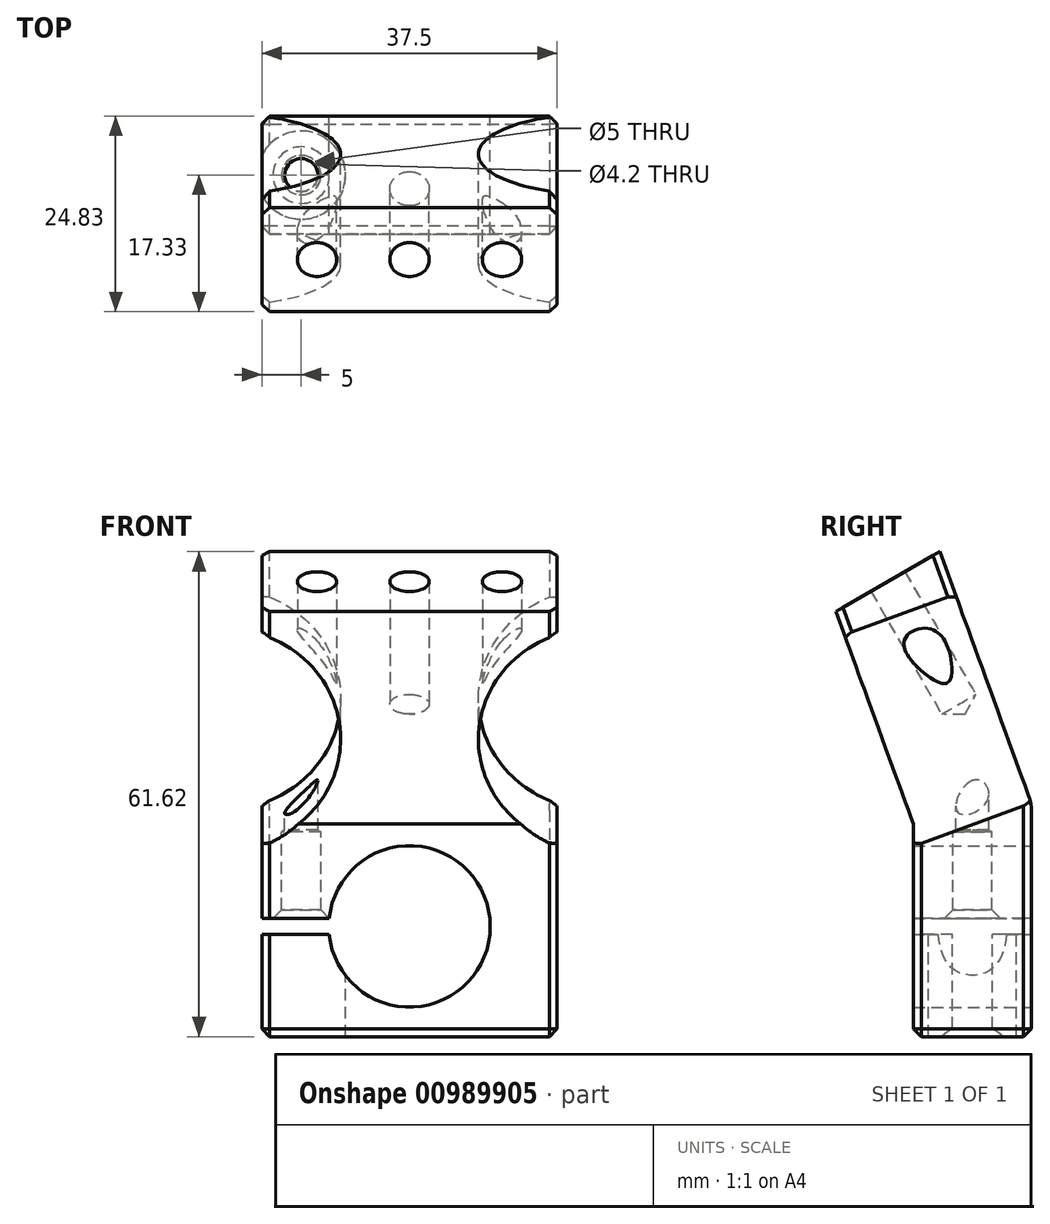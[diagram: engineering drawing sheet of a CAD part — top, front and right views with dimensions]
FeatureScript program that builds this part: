
annotation { "Feature Type Name" : "Feature", "Feature Type Description" : "" }
export const myFeature = defineFeature(function(context is Context, id is Id, definition is map)
    precondition{}
    {
        {
            var Q0;
            Q0=qCreatedBy(makeId("Right.planeOp"),FACE);
            var sketch = newSketch(context, id + "F0", { "sketchPlane" : qUnion([Q0])});
            skLineSegment(sketch, "E0", {"start": v(-9.83, 40) * mm, "end": v(0, 13) * mm});
            skLineSegment(sketch, "E1", {"start": v(0, 13) * mm, "end": v(0, -14) * mm});
            skLineSegment(sketch, "E2", {"start": v(0, -14) * mm, "end": v(15, -14) * mm});
            skLineSegment(sketch, "E3", {"start": v(15, -14) * mm, "end": v(15, 15.64) * mm});
            skLineSegment(sketch, "E4", {"start": v(15, 15.64) * mm, "end": v(3.36, 47.62) * mm});
            skLineSegment(sketch, "E5", {"start": v(-9.83, 40) * mm, "end": v(3.36, 47.62) * mm});
            skSolve(sketch);
        }
        {
            var Q0;
            Q0=makeQuery(id+"F0.imprint","IMPRINT",FACE,{"disambiguationData":[TD([[makeQuery(id+"F0.imprint","IMPRINT",EDGE,{"derivedFrom":sQuery(id+"F0.wireOp",EDGE,"E0")}),1.0]])]});
            extrude(context, id + "F1", {"entities" : qUnion([Q0]), "depth" : 37.5 * mm, "offsetDistance" : 25 * mm, "symmetric" : true});
        }
        {
            var Q0;
            Q0=makeQuery(id+"F1.opExtrude","SWEPT_FACE",FACE,{"disambiguationData":[OSD([sQuery(id+"F0.wireOp",EDGE,"E1")])]});
            var sketch = newSketch(context, id + "F2", { "sketchPlane" : qUnion([Q0])});
            skPoint(sketch, "E6", {"position": v(0, 0) * mm});
            skLineSegment(sketch, "E7.bottom", {"start": v(-18.75, 1) * mm, "end": v(-8.7, 1) * mm});
            skLineSegment(sketch, "E7.top", {"start": v(-18.75, -1) * mm, "end": v(-8.7, -1) * mm});
            skLineSegment(sketch, "E7.left", {"start": v(-18.75, 1) * mm, "end": v(-18.75, -1) * mm});
            skLineSegment(sketch, "E7.right", {"start": v(-8.7, 1) * mm, "end": v(-8.7, -1) * mm});
            skSolve(sketch);
        }
        {
            var Q0;
            Q0=sQuery(id+"F2.wireOp",VERTEX,"E6");
            var Q1;
            Q1=makeQuery(id+"F1.opExtrude","SWEPT_BODY",BODY,{"disambiguationData":[OSD([sQuery(id+"F0.wireOp",EDGE,"E0"),sQuery(id+"F0.wireOp",EDGE,"E1"),sQuery(id+"F0.wireOp",EDGE,"E2"),sQuery(id+"F0.wireOp",EDGE,"E3"),sQuery(id+"F0.wireOp",EDGE,"E4"),sQuery(id+"F0.wireOp",EDGE,"7Aq8HTqt-HB1i-FSIZ-Xick-NeTbkuInXDNU")])]});
            hole(context, id + "F3", {"style" : HoleStyle.SIMPLE, "endStyle" : HoleEndStyle.THROUGH, "holeDiameter" : 20.5 * mm, "majorDiameter" : 4 * mm, "tappedDepth" : 10.1 * mm, "tapClearance" : 3, "locations" : qUnion([Q0]), "scope" : qUnion([Q1]), "startStyle" : HoleStartStyle.PART});
        }
        {
            var Q0;
            Q0 = qSketchRegion(id + "F2", true);
            extrude(context, id + "F4", {"entities" : qUnion([Q0]), "operationType" : NewBodyOperationType.REMOVE, "endBound" : BoundingType.THROUGH_ALL, "oppositeDirection" : true, "depth" : 25 * mm, "offsetDistance" : 25 * mm});
        }
        {
            var Q0;
            Q0=makeQuery(id+"F1.opExtrude","SWEPT_FACE",FACE,{"disambiguationData":[OSD([sQuery(id+"F0.wireOp",EDGE,"E2")])]});
            var sketch = newSketch(context, id + "F5", { "sketchPlane" : qUnion([Q0])});
            skPoint(sketch, "E8", {"position": v(-13.75, -7.5) * mm});
            skSolve(sketch);
        }
        {
            var Q0;
            Q0=sQuery(id+"F5.wireOp",VERTEX,"E8");
            var Q1;
            Q1=makeQuery(id+"F1.opExtrude","SWEPT_BODY",BODY,{"disambiguationData":[OSD([sQuery(id+"F0.wireOp",EDGE,"E0"),sQuery(id+"F0.wireOp",EDGE,"E1"),sQuery(id+"F0.wireOp",EDGE,"E2"),sQuery(id+"F0.wireOp",EDGE,"E3"),sQuery(id+"F0.wireOp",EDGE,"E4"),sQuery(id+"F0.wireOp",EDGE,"7Aq8HTqt-HB1i-FSIZ-Xick-NeTbkuInXDNU")])]});
            hole(context, id + "F6", {"style" : HoleStyle.C_SINK, "endStyle" : HoleEndStyle.BLIND, "standardTappedOrClearance" : lookupTablePath({ "standard" : "ISO", "size" : "5", "type" : "Drilled" }), "standardBlindInLast" : lookupTablePath({ "standard" : "ISO", "size" : "5", "type" : "Drilled" }), "holeDiameter" : 5 * mm, "cSinkDiameter" : 11.2 * mm, "cSinkAngle" : 90 * degree, "majorDiameter" : 5 * mm, "holeDepth" : 13 * mm, "tappedDepth" : 10.1 * mm, "tapClearance" : 3, "locations" : qUnion([Q0]), "scope" : qUnion([Q1]), "startStyle" : HoleStartStyle.PART});
        }
        {
            var Q0;
            Q0=makeQuery(id+"F4.boolean.opBoolean","COPY",FACE,{"derivedFrom":makeQuery(id+"F4.opExtrude","SWEPT_FACE",FACE,{"disambiguationData":[OSD([sQuery(id+"F2.wireOp",EDGE,"E7.bottom")])]})});
            var sketch = newSketch(context, id + "F7", { "sketchPlane" : qUnion([Q0])});
            skPoint(sketch, "E9", {"position": v(-13.75, -7.5) * mm});
            skSolve(sketch);
        }
        {
            var Q0;
            Q0=makeQuery(id+"F1.opExtrude","SWEPT_FACE",FACE,{"disambiguationData":[OSD([sQuery(id+"F0.wireOp",EDGE,"E4")])]});
            var sketch = newSketch(context, id + "F8", { "sketchPlane" : qUnion([Q0])});
            skArc(sketch, "E10", {"start": v(-18.75, 9.57) * mm, "mid": v(-8.75, 23.71) * mm, "end": v(-18.75, 37.86) * mm});
            skArc(sketch, "E11", {"start": v(18.75, 37.86) * mm, "mid": v(8.75, 23.71) * mm, "end": v(18.75, 9.57) * mm});
            skLineSegment(sketch, "E12.0", {"start": v(-18.75, 9.57) * mm, "end": v(-18.75, 9.57) * mm});
            skLineSegment(sketch, "E13.0", {"start": v(18.75, 9.57) * mm, "end": v(18.75, 9.57) * mm});
            skSolve(sketch);
        }
        {
            var Q0;
            Q0=sQuery(id+"F7.wireOp",VERTEX,"E9");
            var Q1;
            Q1=makeQuery(id+"F1.opExtrude","SWEPT_BODY",BODY,{"disambiguationData":[OSD([sQuery(id+"F0.wireOp",EDGE,"E0"),sQuery(id+"F0.wireOp",EDGE,"E1"),sQuery(id+"F0.wireOp",EDGE,"E2"),sQuery(id+"F0.wireOp",EDGE,"E3"),sQuery(id+"F0.wireOp",EDGE,"E4"),sQuery(id+"F0.wireOp",EDGE,"7Aq8HTqt-HB1i-FSIZ-Xick-NeTbkuInXDNU")])]});
            hole(context, id + "F9", {"style" : HoleStyle.SIMPLE, "endStyle" : HoleEndStyle.BLIND, "standardTappedOrClearance" : lookupTablePath({ "standard" : "ISO", "engagement" : "75%", "pitch" : "0.8 mm", "size" : "M5", "type" : "Tapped" }), "standardBlindInLast" : lookupTablePath({ "standard" : "ISO", "fit" : "Normal", "engagement" : "75%", "pitch" : "0.8 mm", "size" : "M5", "type" : "Clearance & tapped" }), "holeDiameter" : 4.2 * mm, "majorDiameter" : 5 * mm, "showTappedDepth" : true, "holeDepth" : 12.4 * mm, "tappedDepth" : 10 * mm, "tapClearance" : 3, "locations" : qUnion([Q0]), "scope" : qUnion([Q1]), "startStyle" : HoleStartStyle.PART});
        }
        {
            var Q0;
            {var subQ0=sQuery(id+"F8.wireOp",EDGE,"E10");Q0=makeQuery(id+"F8.imprint","IMPRINT",FACE,{"disambiguationData":[TD([[makeQuery(id+"F8.imprint","IMPRINT",EDGE,{"derivedFrom":subQ0}),1.0]])]});}
            var Q1;
            {var subQ0=sQuery(id+"F8.wireOp",EDGE,"E11");Q1=makeQuery(id+"F8.imprint","IMPRINT",FACE,{"disambiguationData":[TD([[makeQuery(id+"F8.imprint","IMPRINT",EDGE,{"derivedFrom":subQ0}),1.0]])]});}
            extrude(context, id + "F10", {"entities" : qUnion([Q0, Q1]), "operationType" : NewBodyOperationType.REMOVE, "endBound" : BoundingType.THROUGH_ALL, "oppositeDirection" : true, "depth" : 25 * mm, "offsetDistance" : 25 * mm});
        }
        {
            var Q0;
            Q0=makeQuery(id+"F3.hole-0.boolean.opBoolean","INTERSECT",EDGE,{"derivedFrom":[makeQuery(id+"F1.opExtrude","SWEPT_FACE",FACE,{"disambiguationData":[OSD([sQuery(id+"F0.wireOp",EDGE,"E3")])]}),makeQuery(id+"F3.hole-0.opRevolve","SWEPT_FACE",FACE,{"disambiguationData":[OSD([sQuery(id+"F3.hole-0.sketch.wireOp",EDGE,"core_line_2")])]})]});
            var Q1;
            Q1=makeQuery(id+"F3.hole-0.boolean.opBoolean","COPY",EDGE,{"derivedFrom":makeQuery(id+"F3.hole-0.opRevolve","SWEPT_EDGE",EDGE,{"disambiguationData":[OSD([sQuery(id+"F3.hole-0.sketch.wireOp",EDGE,"core_line_2"),sQuery(id+"F3.hole-0.sketch.wireOp",EDGE,"core_line_3")])]})});
            var Q2;
            Q2=makeQuery(id+"F1.opExtrude","CAP_EDGE",EDGE,{"disambiguationData":[OSD([sQuery(id+"F0.wireOp",EDGE,"E2")])],"isStart":false});
            var Q3;
            {var subQ0=sQuery(id+"F0.wireOp",EDGE,"E3");var subQ1=sQuery(id+"F0.wireOp",EDGE,"E2");Q3=makeQuery(id+"F6.hole-0.boolean.opBoolean","SPLIT",EDGE,{"disambiguationData":[TD([makeQuery(id+"F1.opExtrude","SWEPT_FACE",FACE,{"disambiguationData":[OSD([subQ0])]})])],"derivedFrom":makeQuery(id+"F1.opExtrude","CAP_EDGE",EDGE,{"disambiguationData":[OSD([subQ1])],"isStart":true})});}
            var Q4;
            {var subQ0=sQuery(id+"F0.wireOp",EDGE,"E2");var subQ1=sQuery(id+"F0.wireOp",EDGE,"E1");Q4=makeQuery(id+"F6.hole-0.boolean.opBoolean","SPLIT",EDGE,{"disambiguationData":[TD([makeQuery(id+"F1.opExtrude","SWEPT_FACE",FACE,{"disambiguationData":[OSD([subQ1])]})])],"derivedFrom":makeQuery(id+"F1.opExtrude","CAP_EDGE",EDGE,{"disambiguationData":[OSD([subQ0])],"isStart":true})});}
            var Q5;
            Q5=makeQuery(id+"F1.opExtrude","CAP_EDGE",EDGE,{"disambiguationData":[OSD([sQuery(id+"F0.wireOp",EDGE,"E1")])],"isStart":false});
            var Q6;
            Q6=makeQuery(id+"F1.opExtrude","CAP_EDGE",EDGE,{"disambiguationData":[OSD([sQuery(id+"F0.wireOp",EDGE,"E3")])],"isStart":false});
            var Q7;
            {var subQ0=sQuery(id+"F0.wireOp",EDGE,"E4");var subQ1=sQuery(id+"F0.wireOp",EDGE,"E3");Q7=makeQuery(id+"F4.boolean.opBoolean","SPLIT",EDGE,{"disambiguationData":[TD([makeQuery(id+"F1.opExtrude","SWEPT_FACE",FACE,{"disambiguationData":[OSD([subQ0])]})])],"derivedFrom":makeQuery(id+"F1.opExtrude","CAP_EDGE",EDGE,{"disambiguationData":[OSD([subQ1])],"isStart":true})});}
            var Q8;
            {var subQ0=sQuery(id+"F0.wireOp",EDGE,"E3");var subQ1=sQuery(id+"F0.wireOp",EDGE,"E2");Q8=makeQuery(id+"F4.boolean.opBoolean","SPLIT",EDGE,{"disambiguationData":[TD([makeQuery(id+"F1.opExtrude","SWEPT_FACE",FACE,{"disambiguationData":[OSD([subQ1])]})])],"derivedFrom":makeQuery(id+"F1.opExtrude","CAP_EDGE",EDGE,{"disambiguationData":[OSD([subQ0])],"isStart":true})});}
            var Q9;
            {var subQ0=sQuery(id+"F0.wireOp",EDGE,"E2");var subQ1=sQuery(id+"F0.wireOp",EDGE,"E1");Q9=makeQuery(id+"F4.boolean.opBoolean","SPLIT",EDGE,{"disambiguationData":[TD([makeQuery(id+"F1.opExtrude","SWEPT_FACE",FACE,{"disambiguationData":[OSD([subQ0])]})])],"derivedFrom":makeQuery(id+"F1.opExtrude","CAP_EDGE",EDGE,{"disambiguationData":[OSD([subQ1])],"isStart":true})});}
            var Q10;
            {var subQ0=sQuery(id+"F0.wireOp",EDGE,"E2");var subQ1=sQuery(id+"F0.wireOp",EDGE,"E1");Q10=makeQuery(id+"F6.hole-0.boolean.opBoolean","SPLIT",EDGE,{"disambiguationData":[TD([makeQuery(id+"F1.opExtrude","CAP_FACE",FACE,{"disambiguationData":[OSD([sQuery(id+"F0.wireOp",EDGE,"E0"),subQ1,subQ0,sQuery(id+"F0.wireOp",EDGE,"E3"),sQuery(id+"F0.wireOp",EDGE,"E4"),sQuery(id+"F0.wireOp",EDGE,"7Aq8HTqt-HB1i-FSIZ-Xick-NeTbkuInXDNU")])],"isStart":false})])],"derivedFrom":makeQuery(id+"F1.opExtrude","SWEPT_EDGE",EDGE,{"disambiguationData":[OSD([subQ1,subQ0])]})});}
            var Q11;
            {var subQ0=sQuery(id+"F0.wireOp",EDGE,"E3");var subQ1=sQuery(id+"F0.wireOp",EDGE,"E2");Q11=makeQuery(id+"F6.hole-0.boolean.opBoolean","SPLIT",EDGE,{"disambiguationData":[TD([makeQuery(id+"F1.opExtrude","CAP_FACE",FACE,{"disambiguationData":[OSD([sQuery(id+"F0.wireOp",EDGE,"E0"),sQuery(id+"F0.wireOp",EDGE,"E1"),subQ1,subQ0,sQuery(id+"F0.wireOp",EDGE,"E4"),sQuery(id+"F0.wireOp",EDGE,"7Aq8HTqt-HB1i-FSIZ-Xick-NeTbkuInXDNU")])],"isStart":false})])],"derivedFrom":makeQuery(id+"F1.opExtrude","SWEPT_EDGE",EDGE,{"disambiguationData":[OSD([subQ1,subQ0])]})});}
            var Q12;
            {var subQ0=sQuery(id+"F0.wireOp",EDGE,"E0");var subQ1=sQuery(id+"F0.wireOp",EDGE,"E1");Q12=makeQuery(id+"F4.boolean.opBoolean","SPLIT",EDGE,{"disambiguationData":[TD([makeQuery(id+"F1.opExtrude","SWEPT_FACE",FACE,{"disambiguationData":[OSD([subQ0])]})])],"derivedFrom":makeQuery(id+"F1.opExtrude","CAP_EDGE",EDGE,{"disambiguationData":[OSD([subQ1])],"isStart":true})});}
            var Q13;
            Q13=makeQuery(id+"F10.boolean.opBoolean","COPY",EDGE,{"derivedFrom":makeQuery(id+"F10.opExtrude","CAP_EDGE",EDGE,{"disambiguationData":[OSD([sQuery(id+"F8.wireOp",EDGE,"E11")])],"isStart":true})});
            var Q14;
            Q14=makeQuery(id+"F10.boolean.opBoolean","COPY",EDGE,{"derivedFrom":makeQuery(id+"F10.opExtrude","CAP_EDGE",EDGE,{"disambiguationData":[OSD([sQuery(id+"F8.wireOp",EDGE,"E10")])],"isStart":true})});
            var Q15;
            Q15=makeQuery(id+"F1.opExtrude","CAP_EDGE",EDGE,{"disambiguationData":[OSD([sQuery(id+"F0.wireOp",EDGE,"E4")])],"isStart":false});
            var Q16;
            Q16=makeQuery(id+"F1.opExtrude","CAP_EDGE",EDGE,{"disambiguationData":[OSD([sQuery(id+"F0.wireOp",EDGE,"E4")])],"isStart":true});
            var Q17;
            Q17=makeQuery(id+"F1.opExtrude","CAP_EDGE",EDGE,{"disambiguationData":[OSD([sQuery(id+"F0.wireOp",EDGE,"E0")])],"isStart":true});
            var Q18;
            Q18=makeQuery(id+"F1.opExtrude","CAP_EDGE",EDGE,{"disambiguationData":[OSD([sQuery(id+"F0.wireOp",EDGE,"E0")])],"isStart":false});
            chamfer(context, id + "F11", {"entities" : qUnion([Q0, Q1, Q2, Q3, Q4, Q5, Q6, Q7, Q8, Q9, Q10, Q11, Q12, Q13, Q14, Q15, Q16, Q17, Q18]), "width" : 1 * mm, "tangentPropagation" : true});
        }
        {
            var Q0;
            Q0=makeQuery(id+"F1.opExtrude","SWEPT_EDGE",EDGE,{"disambiguationData":[OSD([sQuery(id+"F0.wireOp",EDGE,"E3"),sQuery(id+"F0.wireOp",EDGE,"E4")])]});
            fillet(context, id + "F12", {"entities" : qUnion([Q0]), "radius" : 5 * mm, "tangentPropagation" : true, "allowEdgeOverflow" : false});
        }
        {
            var Q0;
            Q0=makeQuery(id+"F1.opExtrude","SWEPT_FACE",FACE,{"disambiguationData":[OSD([sQuery(id+"F0.wireOp",EDGE,"E5")])]});
            var sketch = newSketch(context, id + "F13", { "sketchPlane" : qUnion([Q0])});
            skPoint(sketch, "E14", {"position": v(11.75, 19.1) * mm});
            skPoint(sketch, "E15", {"position": v(0, 19.1) * mm});
            skPoint(sketch, "E16", {"position": v(-11.75, 19.1) * mm});
            skLineSegment(sketch, "E17", {"start": v(-18.75, 19.1) * mm, "end": v(18.75, 19.1) * mm, "construction": true});
            skSolve(sketch);
        }
        {
            var Q0;
            Q0=sQuery(id+"F13.wireOp",VERTEX,"E16");
            var Q1;
            Q1=sQuery(id+"F13.wireOp",VERTEX,"E15");
            var Q2;
            Q2=sQuery(id+"F13.wireOp",VERTEX,"E14");
            var Q3;
            Q3=makeQuery(id+"F1.opExtrude","SWEPT_BODY",BODY,{"disambiguationData":[OSD([sQuery(id+"F0.wireOp",EDGE,"E0"),sQuery(id+"F0.wireOp",EDGE,"E1"),sQuery(id+"F0.wireOp",EDGE,"E2"),sQuery(id+"F0.wireOp",EDGE,"E3"),sQuery(id+"F0.wireOp",EDGE,"E4"),sQuery(id+"F0.wireOp",EDGE,"E5")])]});
            hole(context, id + "F14", {"style" : HoleStyle.SIMPLE, "endStyle" : HoleEndStyle.BLIND, "standardTappedOrClearance" : lookupTablePath({ "standard" : "ISO", "engagement" : "75%", "pitch" : "1 mm", "size" : "M6", "type" : "Tapped" }), "standardBlindInLast" : lookupTablePath({ "standard" : "ISO", "fit" : "Normal", "engagement" : "75%", "pitch" : "1 mm", "size" : "M6", "type" : "Clearance & tapped" }), "holeDiameter" : 5 * mm, "majorDiameter" : 6 * mm, "showTappedDepth" : true, "holeDepth" : 18 * mm, "tappedDepth" : 15 * mm, "tapClearance" : 3, "locations" : qUnion([Q0, Q1, Q2]), "scope" : qUnion([Q3]), "startStyle" : HoleStartStyle.PART});
        }
    });
